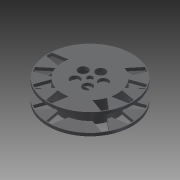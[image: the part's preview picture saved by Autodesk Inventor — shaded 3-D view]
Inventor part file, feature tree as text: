
AUTODESK INVENTOR PART (.ipt)
format: ipt  version: 2014 SP1 (Build 180222100, 222)  size: 237,568 bytes
history: native  units: in
note: dims shown in document units (in); Inventor stores cm internally (conversion verified against a paired STEP export)
features: extrude x7, sketch x7
ambient origin geometry x8: Origin, YZ Plane, XZ Plane, XY Plane, X Axis, Y Axis, Z Axis, Center Point
bodies: Solid1 (feature_tree)
feature tree (14):
  extrude  "Extrusion1"  Depth=0.314in TaperAngle=0.0deg
  extrude  "Extrusion2"  Depth=1.616in TaperAngle=0.0deg
  extrude  "Extrusion3"  Depth=0.314in TaperAngle=0.0deg
  extrude  "Extrusion4"  Depth=1.15in
  extrude  "Extrusion5"  Depth=0.6in
  extrude  "Extrusion6"  Depth=0.3in TaperAngle=360.0deg
  extrude  "Extrusion7"  Depth=1.615in
  sketch  "Sketch1"  dims[d0=9.0in d1=0.314in d2=0.0in]
  sketch  "Sketch2"  dims[d3=5.847in d4=1.616in d5=0.0in]
  sketch  "Sketch3"  dims[d6=9.0in d7=0.314in d8=0.0in]
  sketch  "Sketch4"  dims[d10=5.847in d11=1.15in]
  sketch  "Sketch5"  dims[d12=0.575in d13=0.6in]
  sketch  "Sketch6"  dims[d14=0.3in d15=4.7244in d17=360.0deg]
  sketch  "Sketch7"  dims[d19=500.0in d20=0.0in d21=1.0in d22=1.9685in d24=360.0deg d26=500.0in d27=0.0in d28=1.615in d29=0.0in d30=0.6in d31=6.885in d32=0.0in]
